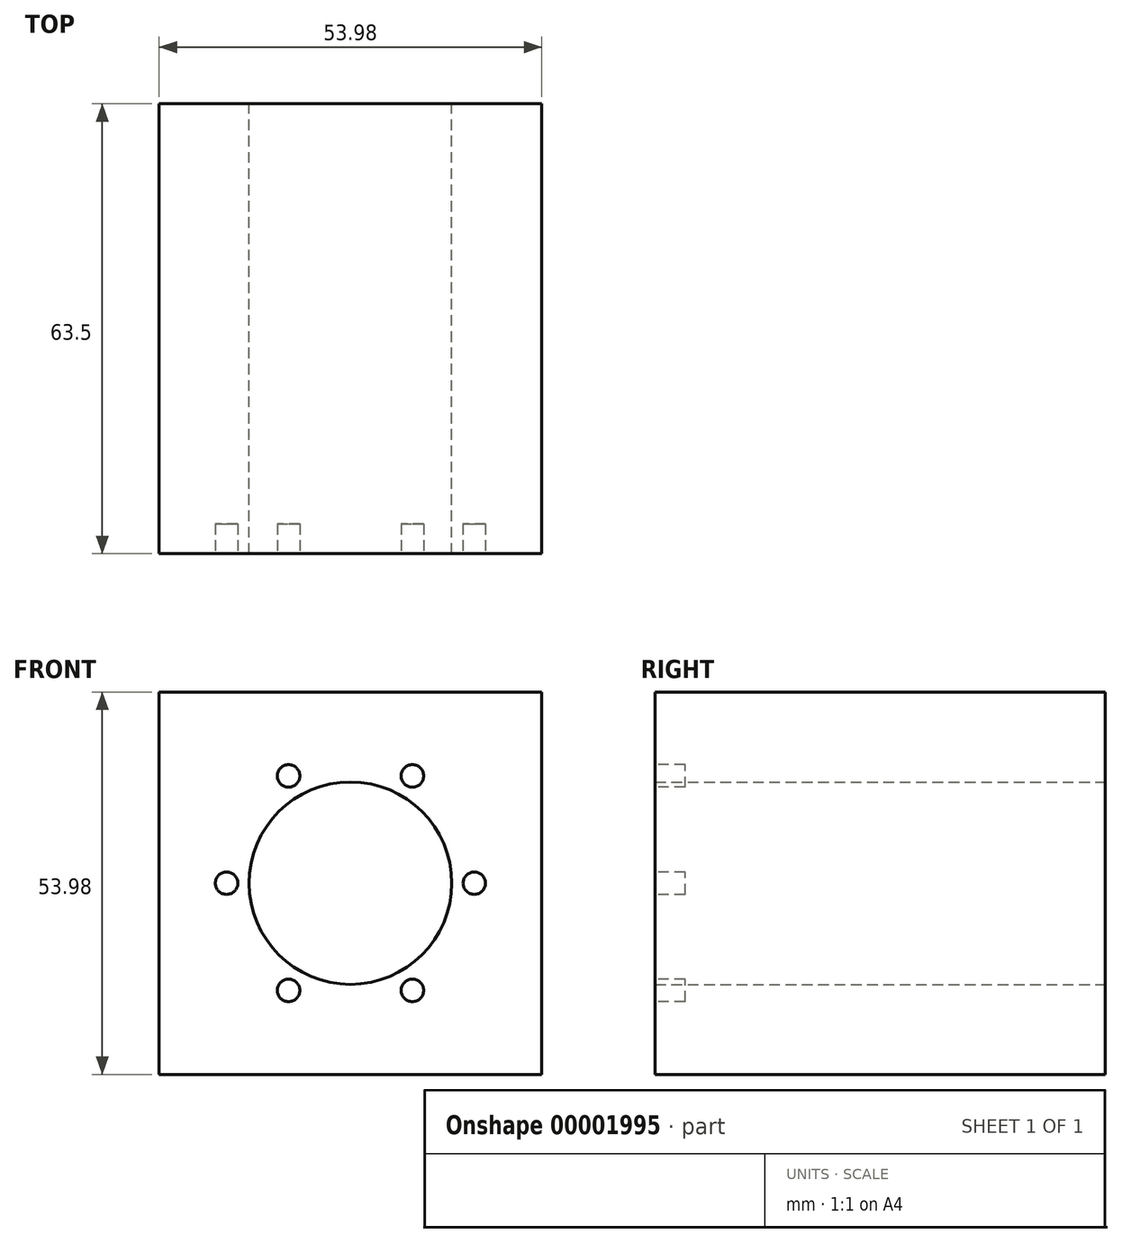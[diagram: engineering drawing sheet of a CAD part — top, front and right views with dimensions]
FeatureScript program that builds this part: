
annotation { "Feature Type Name" : "Feature", "Feature Type Description" : "" }
export const myFeature = defineFeature(function(context is Context, id is Id, definition is map)
    precondition{}
    {
        {
            var Q0;
            Q0=qCreatedBy(makeId("Front.planeOp"),FACE);
            var sketch = newSketch(context, id + "F0", { "sketchPlane" : qUnion([Q0])});
            skLineSegment(sketch, "E0.rect.bottom", {"start": v(26.99, -26.99) * mm, "end": v(-26.99, -26.99) * mm});
            skLineSegment(sketch, "E0.rect.top", {"start": v(26.99, 26.99) * mm, "end": v(-26.99, 26.99) * mm});
            skLineSegment(sketch, "E0.rect.left", {"start": v(26.99, -26.99) * mm, "end": v(26.99, 26.99) * mm});
            skLineSegment(sketch, "E0.rect.right", {"start": v(-26.99, -26.99) * mm, "end": v(-26.99, 26.99) * mm});
            skPoint(sketch, "E0.rect.middle", {"position": v(0, 0) * mm});
            skCircle(sketch, "E1", {"center": v(0, 0) * mm, "radius": 14.29 * mm});
            skSolve(sketch);
        }
        {
            var Q0;
            Q0 = qSketchRegion(id + "F0", true);
            extrude(context, id + "F1", {"entities" : qUnion([Q0]), "endBound" : BoundingType.SYMMETRIC, "depth" : 63.5 * mm});
        }
        {
            var Q0;
            Q0=makeQuery(id+"F1.opExtrude","CAP_FACE",FACE,{"disambiguationData":[OSD([sQuery(id+"F0.wireOp",EDGE,"E0.rect.bottom"),sQuery(id+"F0.wireOp",EDGE,"E0.rect.top"),sQuery(id+"F0.wireOp",EDGE,"E0.rect.left"),sQuery(id+"F0.wireOp",EDGE,"E0.rect.right"),sQuery(id+"F0.wireOp",EDGE,"E1")])],"isStart":false});
            var sketch = newSketch(context, id + "F2", { "sketchPlane" : qUnion([Q0])});
            skCircle(sketch, "E2", {"center": v(-17.48, 0) * mm, "radius": 1.59 * mm});
            skCircle(sketch, "E3.1.0", {"center": v(-8.74, -15.13) * mm, "radius": 1.59 * mm});
            skCircle(sketch, "E3.2.0", {"center": v(8.74, -15.13) * mm, "radius": 1.59 * mm});
            skCircle(sketch, "E3.3.0", {"center": v(17.48, 0) * mm, "radius": 1.59 * mm});
            skCircle(sketch, "E3.4.0", {"center": v(8.74, 15.13) * mm, "radius": 1.59 * mm});
            skCircle(sketch, "E3.5.0", {"center": v(-8.74, 15.13) * mm, "radius": 1.59 * mm});
            skPoint(sketch, "E3.center", {"position": v(0, 0) * mm});
            skSolve(sketch);
        }
        {
            var Q0;
            Q0 = qSketchRegion(id + "F2", true);
            extrude(context, id + "F3", {"entities" : qUnion([Q0]), "operationType" : NewBodyOperationType.REMOVE, "oppositeDirection" : true, "depth" : 4.22 * mm});
        }
    });
